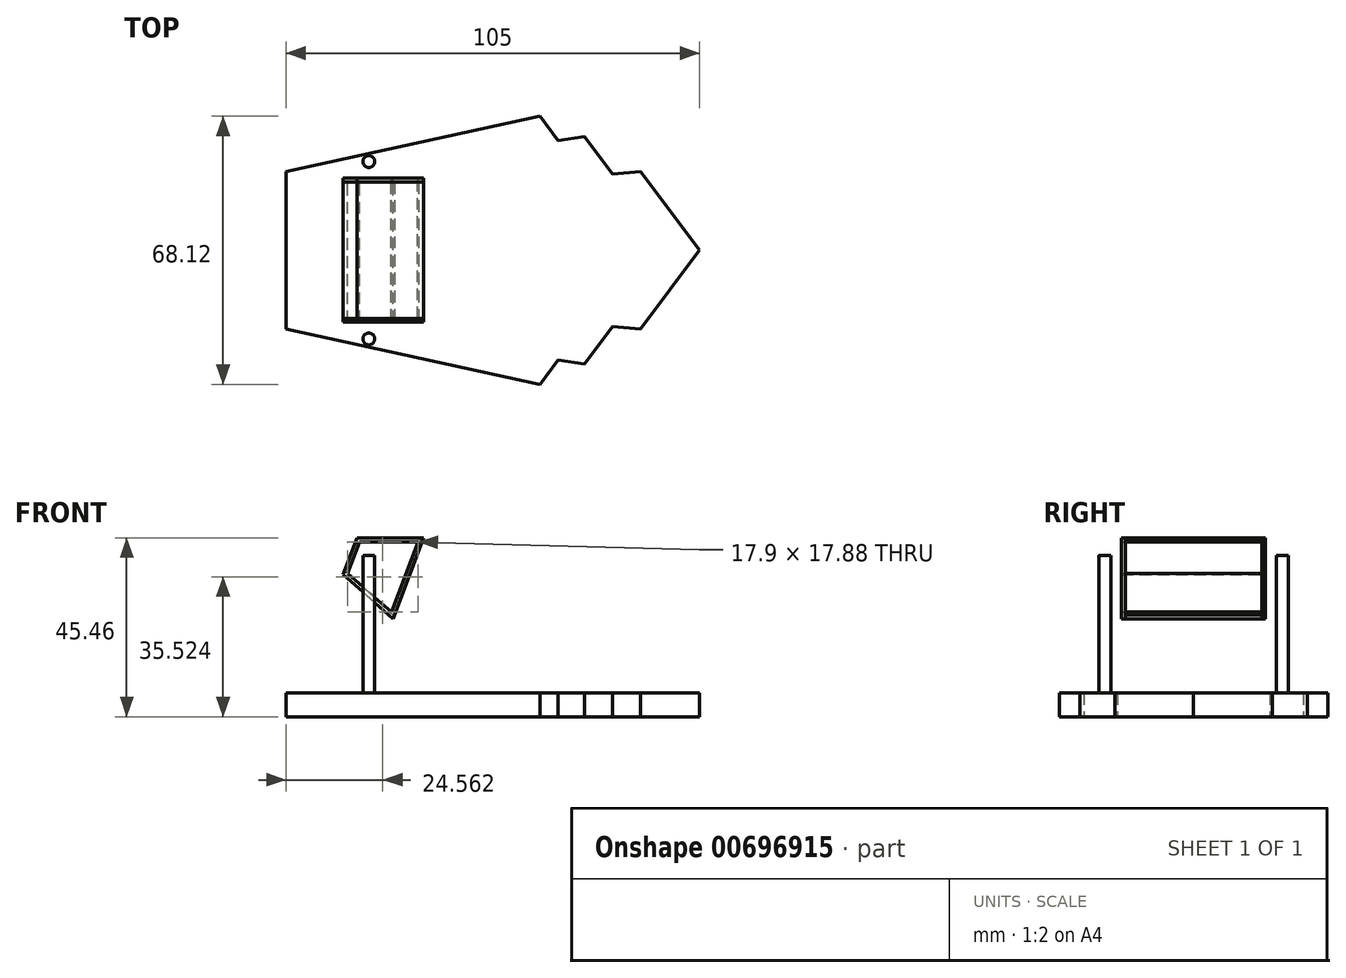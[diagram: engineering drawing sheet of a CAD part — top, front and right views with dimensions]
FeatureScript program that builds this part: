
annotation { "Feature Type Name" : "Feature", "Feature Type Description" : "" }
export const myFeature = defineFeature(function(context is Context, id is Id, definition is map)
    precondition{}
    {
        {
            var Q0;
            Q0=qCreatedBy(makeId("Top.planeOp"),FACE);
            var sketch = newSketch(context, id + "F0", { "sketchPlane" : qUnion([Q0])});
            skLineSegment(sketch, "E0.left", {"start": v(-45, -17.44) * mm, "end": v(-45, -20) * mm, "construction": true});
            skPoint(sketch, "E0.middle", {"position": v(0, 0) * mm});
            skLineSegment(sketch, "E1", {"start": v(45, -20) * mm, "end": v(-45, -12.44) * mm});
            skLineSegment(sketch, "E2", {"start": v(60, 0) * mm, "end": v(45, -20) * mm});
            skPoint(sketch, "E3.orphan", {"position": v(-45, -35.28) * mm});
            skLineSegment(sketch, "E4", {"start": v(-45, -17.44) * mm, "end": v(30.86, -28.85) * mm});
            skLineSegment(sketch, "E5", {"start": v(30.86, -28.85) * mm, "end": v(37.94, -19.4) * mm});
            skLineSegment(sketch, "E6", {"start": v(-45, -20) * mm, "end": v(19.46, -34.06) * mm});
            skPoint(sketch, "E0.bottom.end.orphan", {"position": v(45, 20) * mm});
            skPoint(sketch, "E7.orphan", {"position": v(-45, 20) * mm});
            skLineSegment(sketch, "E8", {"start": v(19.46, -34.06) * mm, "end": v(24.12, -27.83) * mm});
            skPoint(sketch, "E9.orphan", {"position": v(-45, -22.44) * mm});
            skLineSegment(sketch, "E10", {"start": v(-45, -20) * mm, "end": v(-45, 0) * mm});
            skLineSegment(sketch, "E11", {"start": v(-45, 0) * mm, "end": v(60, 0) * mm});
            skSolve(sketch);
        }
        {
            var Q0;
            {var subQ0=sQuery(id+"F0.wireOp",EDGE,"E2");Q0=makeQuery(id+"F0.imprint","IMPRINT",FACE,{"disambiguationData":[TD([[makeQuery(id+"F0.imprint","IMPRINT",EDGE,{"derivedFrom":subQ0}),-1.0]])]});}
            var Q1;
            {var subQ0=sQuery(id+"F0.wireOp",EDGE,"E5");Q1=makeQuery(id+"F0.imprint","IMPRINT",FACE,{"disambiguationData":[TD([[makeQuery(id+"F0.imprint","IMPRINT",EDGE,{"derivedFrom":subQ0}),1.0]])]});}
            var Q2;
            {var subQ4=sQuery(id+"F0.wireOp",EDGE,"E6");Q2=makeQuery(id+"F0.imprint","IMPRINT",FACE,{"disambiguationData":[TD([[makeQuery(id+"F0.imprint","IMPRINT",EDGE,{"derivedFrom":subQ4}),1.0]])]});}
            extrude(context, id + "F1", {"entities" : qUnion([Q0, Q1, Q2]), "depth" : 6 * mm, "offsetDistance" : 25 * mm});
        }
        {
            var Q0;
            Q0=makeQuery(id+"F1.opExtrude","SWEPT_BODY",BODY,{"disambiguationData":[OSD([sQuery(id+"F0.wireOp",EDGE,"E1"),sQuery(id+"F0.wireOp",EDGE,"E2"),sQuery(id+"F0.wireOp",EDGE,"E4"),sQuery(id+"F0.wireOp",EDGE,"E5"),sQuery(id+"F0.wireOp",EDGE,"E6"),sQuery(id+"F0.wireOp",EDGE,"E8"),sQuery(id+"F0.wireOp",EDGE,"E10"),sQuery(id+"F0.wireOp",EDGE,"E11")])]});
            var Q1;
            Q1=qCreatedBy(makeId("Front.planeOp"),FACE);
            mirror(context, id + "F2", {"operationType" : NewBodyOperationType.ADD, "entities" : qUnion([Q0]), "mirrorPlane" : qUnion([Q1])});
        }
        {
            var Q0;
            {var subQ0=makeQuery(id+"F1.opExtrude","CAP_FACE",FACE,{"disambiguationData":[OSD([sQuery(id+"F0.wireOp",EDGE,"E1"),sQuery(id+"F0.wireOp",EDGE,"E2"),sQuery(id+"F0.wireOp",EDGE,"E4"),sQuery(id+"F0.wireOp",EDGE,"E5"),sQuery(id+"F0.wireOp",EDGE,"E6"),sQuery(id+"F0.wireOp",EDGE,"E8"),sQuery(id+"F0.wireOp",EDGE,"E10"),sQuery(id+"F0.wireOp",EDGE,"E11")])],"isStart":false});Q0=makeQuery(id+"F2.boolean.opBoolean","MERGE",FACE,{"derivedFrom":[subQ0,makeQuery(id+"F2.opPattern","COPY",FACE,{"derivedFrom":subQ0,"instanceName":"1"})]});}
            var sketch = newSketch(context, id + "F3", { "sketchPlane" : qUnion([Q0])});
            skLineSegment(sketch, "E12", {"start": v(24.12, -27.83) * mm, "end": v(-45, -17.44) * mm});
            skLineSegment(sketch, "E13", {"start": v(37.94, -19.4) * mm, "end": v(-45, -12.54) * mm});
            skLineSegment(sketch, "E14", {"start": v(24.12, 27.83) * mm, "end": v(-45, 17.44) * mm});
            skLineSegment(sketch, "E15", {"start": v(37.94, 19.4) * mm, "end": v(-45, 12.54) * mm});
            skSolve(sketch);
        }
        {
            var Q0;
            {var subQ0=sQuery(id+"F3.wireOp",EDGE,"E12");Q0=makeQuery(id+"F3.imprint","IMPRINT",FACE,{"disambiguationData":[TD([[makeQuery(id+"F3.imprint","IMPRINT",EDGE,{"derivedFrom":subQ0}),1.0]])]});}
            var sketch = newSketch(context, id + "F4", { "sketchPlane" : qUnion([Q0])});
            skCircle(sketch, "E16", {"center": v(-24, -22.53) * mm, "radius": 1.5 * mm});
            skCircle(sketch, "E17", {"center": v(-24, 22.53) * mm, "radius": 1.5 * mm});
            skSolve(sketch);
        }
        {
            var Q0;
            Q0=makeQuery(id+"F4.imprint","IMPRINT",FACE,{"disambiguationData":[TD([[makeQuery(id+"F4.imprint","IMPRINT",EDGE,{"derivedFrom":sQuery(id+"F4.wireOp",EDGE,"E16")}),1.0]])]});
            var Q1;
            Q1=makeQuery(id+"F4.imprint","IMPRINT",FACE,{"disambiguationData":[TD([[makeQuery(id+"F4.imprint","IMPRINT",EDGE,{"derivedFrom":sQuery(id+"F4.wireOp",EDGE,"E17")}),1.0]])]});
            extrude(context, id + "F5", {"entities" : qUnion([Q0, Q1]), "operationType" : NewBodyOperationType.ADD, "depth" : 35 * mm, "offsetDistance" : 25 * mm});
        }
        {
            var Q0;
            Q0=qCreatedBy(makeId("Front.planeOp"),FACE);
            cPlane(context, id + "F6", {"entities" : qUnion([Q0]), "cplaneType" : CPlaneType.OFFSET, "offset" : 22.6 * mm, "width" : 150 * mm, "height" : 150 * mm});
        }
        {
            var Q0;
            Q0=qCreatedBy(id+"F6.planeOp",FACE);
            var sketch = newSketch(context, id + "F7", { "sketchPlane" : qUnion([Q0])});
            skCircle(sketch, "E18", {"center": v(-24.01, 39) * mm, "radius": 1.43 * mm});
            skSolve(sketch);
        }
        {
            var Q0;
            Q0=sQuery(id+"F7.wireOp",EDGE,"E18");
            extrude(context, id + "F8", {"bodyType" : ToolBodyType.SURFACE, "surfaceEntities" : qUnion([Q0]), "oppositeDirection" : true, "depth" : 4.7 * mm, "offsetDistance" : 25 * mm});
        }
        {
            var Q0;
            Q0=makeQuery(id+"F8.opExtrude","SWEPT_BODY",BODY,{"disambiguationData":[OSD([sQuery(id+"F7.wireOp",EDGE,"E18")])]});
            var Q1;
            Q1=qCreatedBy(makeId("Front.planeOp"),FACE);
            mirror(context, id + "F9", {"entities" : qUnion([Q0]), "mirrorPlane" : qUnion([Q1])});
        }
        {
            var Q0;
            Q0=qCreatedBy(makeId("Front.planeOp"),FACE);
            cPlane(context, id + "F10", {"entities" : qUnion([Q0]), "cplaneType" : CPlaneType.OFFSET, "offset" : 18.3 * mm, "oppositeDirection" : true, "width" : 150 * mm, "height" : 150 * mm});
        }
        {
            var Q0;
            Q0=qCreatedBy(id+"F10.planeOp",FACE);
            var sketch = newSketch(context, id + "F11", { "sketchPlane" : qUnion([Q0])});
            skLineSegment(sketch, "E19", {"start": v(-27.04, 45.46) * mm, "end": v(-30.57, 36.1) * mm});
            skLineSegment(sketch, "E20", {"start": v(-30.57, 36.1) * mm, "end": v(-17.8, 24.88) * mm});
            skLineSegment(sketch, "E21", {"start": v(-17.8, 24.88) * mm, "end": v(-10.04, 45.46) * mm});
            skLineSegment(sketch, "E22", {"start": v(-10.04, 45.46) * mm, "end": v(-27.04, 45.46) * mm});
            skLineSegment(sketch, "E23", {"start": v(-26.35, 44.46) * mm, "end": v(-11.49, 44.46) * mm});
            skLineSegment(sketch, "E24", {"start": v(-11.49, 44.46) * mm, "end": v(-18.23, 26.58) * mm});
            skLineSegment(sketch, "E25", {"start": v(-18.23, 26.58) * mm, "end": v(-29.4, 36.4) * mm});
            skLineSegment(sketch, "E26", {"start": v(-29.4, 36.4) * mm, "end": v(-26.35, 44.46) * mm});
            skSolve(sketch);
        }
        {
            var Q0;
            Q0=makeQuery(id+"F11.imprint","IMPRINT",FACE,{"disambiguationData":[TD([[makeQuery(id+"F11.imprint","IMPRINT",EDGE,{"derivedFrom":sQuery(id+"F11.wireOp",EDGE,"E19")}),1.0]])]});
            var Q1;
            Q1=makeQuery(id+"F11.imprint","IMPRINT",FACE,{"disambiguationData":[TD([[makeQuery(id+"F11.imprint","IMPRINT",EDGE,{"derivedFrom":sQuery(id+"F11.wireOp",EDGE,"E23")}),-1.0]])]});
            extrude(context, id + "F12", {"entities" : qUnion([Q0, Q1]), "depth" : 1 * mm, "offsetDistance" : 25 * mm});
        }
        {
            var Q0;
            Q0=makeQuery(id+"F12.opExtrude","SWEPT_BODY",BODY,{"disambiguationData":[OSD([sQuery(id+"F11.wireOp",EDGE,"E19"),sQuery(id+"F11.wireOp",EDGE,"E20"),sQuery(id+"F11.wireOp",EDGE,"E21"),sQuery(id+"F11.wireOp",EDGE,"E22")])]});
            var Q1;
            Q1=qCreatedBy(makeId("Front.planeOp"),FACE);
            mirror(context, id + "F13", {"entities" : qUnion([Q0]), "mirrorPlane" : qUnion([Q1])});
        }
        {
            var Q0;
            Q0=makeQuery(id+"F11.imprint","IMPRINT",FACE,{"disambiguationData":[TD([[makeQuery(id+"F11.imprint","IMPRINT",EDGE,{"derivedFrom":sQuery(id+"F11.wireOp",EDGE,"E19")}),1.0]])]});
            var Q1;
            Q1=makeQuery(id+"F13.opPattern","COPY",FACE,{"derivedFrom":makeQuery(id+"F12.opExtrude","CAP_FACE",FACE,{"disambiguationData":[OSD([sQuery(id+"F11.wireOp",EDGE,"E19"),sQuery(id+"F11.wireOp",EDGE,"E20"),sQuery(id+"F11.wireOp",EDGE,"E21"),sQuery(id+"F11.wireOp",EDGE,"E22")])],"isStart":true}),"instanceName":"1"});
            extrude(context, id + "F14", {"entities" : qUnion([Q0]), "endBound" : BoundingType.UP_TO_SURFACE, "depth" : 25 * mm, "endBoundEntityFace" : qUnion([Q1]), "offsetDistance" : 25 * mm});
        }
        {
            var Q0;
            Q0=makeQuery(id+"F14.opExtrude","SWEPT_FACE",FACE,{"disambiguationData":[OSD([sQuery(id+"F11.wireOp",EDGE,"E21")])]});
            var sketch = newSketch(context, id + "F15", { "sketchPlane" : qUnion([Q0])});
            skLineSegment(sketch, "E27.bottom", {"start": v(17.3, 18) * mm, "end": v(-17.3, 18) * mm});
            skLineSegment(sketch, "E27.top", {"start": v(17.3, 38) * mm, "end": v(-17.3, 38) * mm});
            skLineSegment(sketch, "E27.left", {"start": v(17.3, 18) * mm, "end": v(17.3, 38) * mm});
            skLineSegment(sketch, "E27.right", {"start": v(-17.3, 18) * mm, "end": v(-17.3, 38) * mm});
            skPoint(sketch, "E27.middle", {"position": v(0, 28) * mm});
            skSolve(sketch);
        }
        {
            var Q0;
            Q0=makeQuery(id+"F15.imprint","IMPRINT",FACE,{"disambiguationData":[TD([[makeQuery(id+"F15.imprint","IMPRINT",EDGE,{"derivedFrom":sQuery(id+"F15.wireOp",EDGE,"E27.bottom")}),-1.0]])]});
            extrude(context, id + "F16", {"entities" : qUnion([Q0]), "operationType" : NewBodyOperationType.REMOVE, "oppositeDirection" : true, "depth" : 1.1 * mm, "offsetDistance" : 25 * mm});
        }
        {
            var Q0;
            Q0=makeQuery(id+"F5.opExtrude","CAP_FACE",FACE,{"disambiguationData":[OSD([sQuery(id+"F4.wireOp",EDGE,"E16")])],"isStart":false});
            extrude(context, id + "F17", {"entities" : qUnion([Q0]), "operationType" : NewBodyOperationType.ADD, "oppositeDirection" : true, "depth" : 39.7 * mm, "offsetDistance" : 25 * mm});
        }
        {
            var Q0;
            Q0=makeQuery(id+"F5.opExtrude","CAP_FACE",FACE,{"disambiguationData":[OSD([sQuery(id+"F4.wireOp",EDGE,"E17")])],"isStart":false});
            extrude(context, id + "F18", {"entities" : qUnion([Q0]), "operationType" : NewBodyOperationType.ADD, "oppositeDirection" : true, "depth" : 40.4 * mm, "offsetDistance" : 25 * mm});
        }
    });
